# Revit family: Electronics_Controllers_Biamp_Vocia_General-Purpose-I-O-Device_GPIO-1__
name_source: partatom
category: Communication Devices
units: mm (PartAtom-declared; Revit-internal decimal feet)

## family parameters
Cut with Voids When Loaded = No
Host = Face
Maintain Annotation Orientation = No
OmniClass Number = 23.85.10.11.11
OmniClass Title = Sound and Signal Devices
Part Type = Normal
Room Calculation Point = No
Round Connector Dimension = Use Diameter
Shared = No

## types (1)
- GPIO-1
    Altitude = 0-10,000 ft (0-3000m) MSL
    Apparent Load = 0 VA
    Compliance = EN 54-16 Certifed, FCC Part 15B (USA), CE marked (Europe), RoHS Directive (Europe)
    Connector Description = RJ-45 PoE 802.3af Class 3; Primary
    Current Limit = 0.8A
    Default Elevation = 48 "
    Depth = 5 "
    Description = Vocia® GPIO-1 General Purpose I/O Device
    General Purpose Inputs - Quantity = 16
    General Purpose Outputs - Quantity = 16
    General Purpose Outputs - Type = FET Switch, open drain  (low side driver)
    Height = 1.6 "
    High Range Logic High = 12-30V DC
    High Range Logic Low = 0-8V DC
    Housing Material = Biamp - Metal - Silver
    Humidity = 0-95% relative humidity (non-condensing)
    Input Isolation = 500V RMS
    Input Transient Protection = ± 8kV Peak
    Manufacturer = Biamp
    Max Continuous Current = 0.35V
    Max External Supply = 30V DC
    Max Power Consumption = 0 W
    Model = Vocia GPIO-1
    Network Connection = Dual RJ45 with shielded Ethernet (CAT5, CAT5e, CAT6, or CAT7)
    Number of Poles = 1
    Power Factor = 1
    Product Documentation Link = https://downloads.biamp.com
    Product Page URL = https://www.biamp.com
    Product data url = https://www.bimobject.com
    TTL Logic High = 2-5V
    TTL Logic Low = 0 – 0.8V
    Temperature Range = 23 - 104° F (-5 - 40° C)
    URL = https://www.biamp.com
    VMon Input Shutdown = 35V DC
    Voltage = 0 V
    Voltage Monitor = 4-30V DC
    Weight = 2.60 lbf
    Width = 12.5 "

## geometry (parser evidence)
native form markers: Sweep x2
no freeform markers — native parametric forms only
